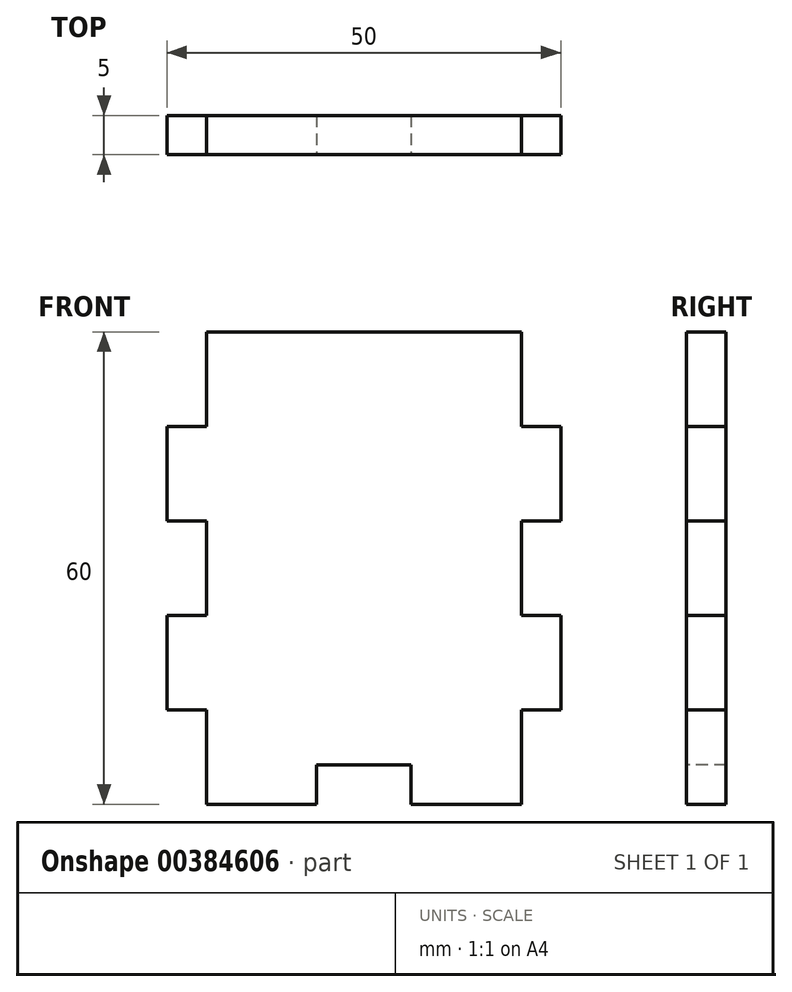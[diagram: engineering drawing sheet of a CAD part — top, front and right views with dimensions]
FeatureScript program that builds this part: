
annotation { "Feature Type Name" : "Feature", "Feature Type Description" : "" }
export const myFeature = defineFeature(function(context is Context, id is Id, definition is map)
    precondition{}
    {
        {
            assignVariable(context, id + "F0", {"name" : "epaisseur", "anyValue" : 5});
        }
        {
            var Q0;
            Q0=qCreatedBy(makeId("Front.planeOp"),FACE);
            var sketch = newSketch(context, id + "F1", { "sketchPlane" : qUnion([Q0])});
            skLineSegment(sketch, "E0.bottom", {"start": v(0, 0) * mm, "end": v(50, 0) * mm});
            skLineSegment(sketch, "E0.top", {"start": v(0, 60) * mm, "end": v(50, 60) * mm});
            skLineSegment(sketch, "E0.left", {"start": v(0, 0) * mm, "end": v(0, 60) * mm});
            skLineSegment(sketch, "E0.right", {"start": v(50, 0) * mm, "end": v(50, 60) * mm});
            skSolve(sketch);
        }
        {
            var Q0;
            Q0=makeQuery(id+"F1.imprint","IMPRINT",FACE,{"disambiguationData":[TD([[makeQuery(id+"F1.imprint","IMPRINT",EDGE,{"derivedFrom":sQuery(id+"F1.wireOp",EDGE,"E0.bottom")}),1.0]])]});
            extrude(context, id + "F2", {"entities" : qUnion([Q0]), "depth" : (getVariable(context, 'epaisseur')) * mm});
        }
        {
            var Q0;
            Q0=makeQuery(id+"F2.opExtrude","CAP_FACE",FACE,{"disambiguationData":[OSD([sQuery(id+"F1.wireOp",EDGE,"E0.bottom"),sQuery(id+"F1.wireOp",EDGE,"E0.top"),sQuery(id+"F1.wireOp",EDGE,"E0.left"),sQuery(id+"F1.wireOp",EDGE,"E0.right")])],"isStart":false});
            var sketch = newSketch(context, id + "F3", { "sketchPlane" : qUnion([Q0])});
            skLineSegment(sketch, "E1.bottom", {"start": v(0, 60) * mm, "end": v(5, 60) * mm});
            skLineSegment(sketch, "E1.top", {"start": v(0, 48) * mm, "end": v(5, 48) * mm});
            skLineSegment(sketch, "E1.left", {"start": v(0, 60) * mm, "end": v(0, 48) * mm});
            skLineSegment(sketch, "E1.right", {"start": v(5, 60) * mm, "end": v(5, 48) * mm});
            skLineSegment(sketch, "E2.bottom", {"start": v(0, 36) * mm, "end": v(5, 36) * mm});
            skLineSegment(sketch, "E2.top", {"start": v(0, 24) * mm, "end": v(5, 24) * mm});
            skLineSegment(sketch, "E2.left", {"start": v(0, 36) * mm, "end": v(0, 24) * mm});
            skLineSegment(sketch, "E2.right", {"start": v(5, 36) * mm, "end": v(5, 24) * mm});
            skLineSegment(sketch, "E3.bottom", {"start": v(0, 0) * mm, "end": v(5, 0) * mm});
            skLineSegment(sketch, "E3.top", {"start": v(0, 12) * mm, "end": v(5, 12) * mm});
            skLineSegment(sketch, "E3.left", {"start": v(0, 0) * mm, "end": v(0, 12) * mm});
            skLineSegment(sketch, "E3.right", {"start": v(5, 0) * mm, "end": v(5, 12) * mm});
            skLineSegment(sketch, "E4", {"start": v(0, 48) * mm, "end": v(0, 36) * mm, "construction": true});
            skLineSegment(sketch, "E5", {"start": v(0, 24) * mm, "end": v(0, 12) * mm, "construction": true});
            skLineSegment(sketch, "E6.bottom", {"start": v(19, 5) * mm, "end": v(31, 5) * mm});
            skLineSegment(sketch, "E6.top", {"start": v(19, 0) * mm, "end": v(31, 0) * mm});
            skLineSegment(sketch, "E6.left", {"start": v(19, 5) * mm, "end": v(19, 0) * mm});
            skLineSegment(sketch, "E6.right", {"start": v(31, 5) * mm, "end": v(31, 0) * mm});
            skLineSegment(sketch, "E7", {"start": v(25, 60) * mm, "end": v(25, 0) * mm, "construction": true});
            skPoint(sketch, "E7.startSnap0", {"position": v(25, 60) * mm});
            skPoint(sketch, "E7.endSnap0", {"position": v(25, 0) * mm});
            skLineSegment(sketch, "E8.MirrorCS", {"start": v(50, 12) * mm, "end": v(45, 12) * mm});
            skLineSegment(sketch, "E9.MirrorCS", {"start": v(50, 0) * mm, "end": v(45, 0) * mm});
            skLineSegment(sketch, "E10.MirrorCS", {"start": v(50, 24) * mm, "end": v(45, 24) * mm});
            skLineSegment(sketch, "E11.MirrorCS", {"start": v(50, 60) * mm, "end": v(45, 60) * mm});
            skLineSegment(sketch, "E12.MirrorCS", {"start": v(50, 48) * mm, "end": v(45, 48) * mm});
            skLineSegment(sketch, "E13.MirrorCS", {"start": v(50, 36) * mm, "end": v(45, 36) * mm});
            skLineSegment(sketch, "E14.MirrorCS", {"start": v(50, 0) * mm, "end": v(50, 12) * mm});
            skLineSegment(sketch, "E15.MirrorCS", {"start": v(50, 24) * mm, "end": v(50, 12) * mm, "construction": true});
            skLineSegment(sketch, "E16.MirrorCS", {"start": v(50, 48) * mm, "end": v(50, 36) * mm, "construction": true});
            skLineSegment(sketch, "E17.MirrorCS", {"start": v(50, 36) * mm, "end": v(50, 24) * mm});
            skLineSegment(sketch, "E18.MirrorCS", {"start": v(45, 0) * mm, "end": v(45, 12) * mm});
            skLineSegment(sketch, "E19.MirrorCS", {"start": v(50, 60) * mm, "end": v(50, 48) * mm});
            skLineSegment(sketch, "E20.MirrorCS", {"start": v(45, 36) * mm, "end": v(45, 24) * mm});
            skLineSegment(sketch, "E21.MirrorCS", {"start": v(45, 60) * mm, "end": v(45, 48) * mm});
            skSolve(sketch);
        }
        {
            var Q0;
            Q0 = qSketchRegion(id + "F3", true);
            extrude(context, id + "F4", {"entities" : qUnion([Q0]), "operationType" : NewBodyOperationType.REMOVE, "oppositeDirection" : true, "depth" : (getVariable(context, 'epaisseur')) * mm});
        }
    });
